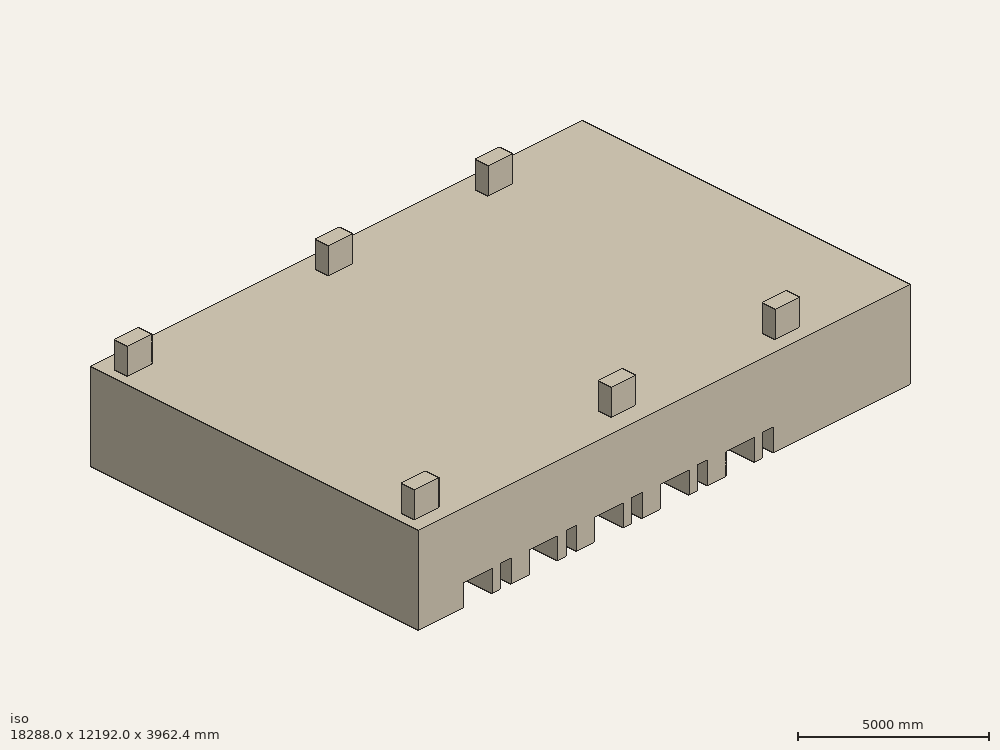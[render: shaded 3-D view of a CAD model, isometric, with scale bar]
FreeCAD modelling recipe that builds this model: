
FCSTD DOCUMENT  (FreeCAD 0.18R14555 (Git shallow))
Label: flow_domain
License: All rights reserved
LicenseURL: http://en.wikipedia.org/wiki/All_rights_reserved
objects: Part::Box×18, Part::MultiFuse×10, Part::Mirroring×1, Part::Cut×1
note: 30 computed .brp shape members not serialized (recipe doc carries the construction recipe); baked Part::Feature solids carry a one-line shape summary decoded from their .brp

FEATURE [Part::Box] Box  label="Room"
  AttacherType = Attacher::AttachEngine3D
  Height = 3048
  Length = 18288
  Width = 12192
FEATURE [Part::Box] Box001  label="Bed 1"
  AttacherType = Attacher::AttachEngine3D
  Height = 762
  Length = 1066.8
  Width = 1981.2
FEATURE [Part::Box] Box002  label="Table 1"
  AttacherType = Attacher::AttachEngine3D
  Height = 798.576
  Length = 396.24
  Placement = pos=(1371.6,0,0) rot=(0,0,1;0rad)
  Width = 396.24
FEATURE [Part::MultiFuse] Fusion  label="Set 1"
  Shapes = -> [Box002,Box001]
FEATURE [Part::Box] Box003  label="Bed 002"
  AttacherType = Attacher::AttachEngine3D
  Height = 762
  Length = 1066.8
  Width = 1981.2
FEATURE [Part::Box] Box004  label="Table 002"
  AttacherType = Attacher::AttachEngine3D
  Height = 798.576
  Length = 396.24
  Placement = pos=(1371.6,0,0) rot=(0,0,1;0rad)
  Width = 396.24
FEATURE [Part::MultiFuse] Fusion001  label="Set 2"
  Placement = pos=(2438.4,0,0) rot=(0,0,1;0rad)
  Shapes = -> [Box004,Box003]
FEATURE [Part::Box] Box005  label="Table 003"
  AttacherType = Attacher::AttachEngine3D
  Height = 798.576
  Length = 396.24
  Placement = pos=(1371.6,0,0) rot=(0,0,1;0rad)
  Width = 396.24
FEATURE [Part::Box] Box006  label="Bed 003"
  AttacherType = Attacher::AttachEngine3D
  Height = 762
  Length = 1066.8
  Width = 1981.2
FEATURE [Part::MultiFuse] Fusion002  label="Set 3"
  Placement = pos=(4876.8,0,0) rot=(0,0,1;0rad)
  Shapes = -> [Box005,Box006]
FEATURE [Part::Box] Box007  label="Bed 004"
  AttacherType = Attacher::AttachEngine3D
  Height = 762
  Length = 1066.8
  Width = 1981.2
FEATURE [Part::Box] Box008  label="Table 004"
  AttacherType = Attacher::AttachEngine3D
  Height = 798.576
  Length = 396.24
  Placement = pos=(1371.6,0,0) rot=(0,0,1;0rad)
  Width = 396.24
FEATURE [Part::MultiFuse] Fusion003  label="Set 4"
  Placement = pos=(7315.2,0,0) rot=(0,0,1;0rad)
  Shapes = -> [Box008,Box007]
FEATURE [Part::Box] Box009  label="Table 005"
  AttacherType = Attacher::AttachEngine3D
  Height = 798.576
  Length = 396.24
  Placement = pos=(1371.6,0,0) rot=(0,0,1;0rad)
  Width = 396.24
FEATURE [Part::Box] Box010  label="Bed 005"
  AttacherType = Attacher::AttachEngine3D
  Height = 762
  Length = 1066.8
  Width = 1981.2
FEATURE [Part::MultiFuse] Fusion004  label="Set 5"
  Placement = pos=(9753.6,0,0) rot=(0,0,1;0rad)
  Shapes = -> [Box009,Box010]
FEATURE [Part::MultiFuse] Fusion005  label="right beds"
  Shapes = -> [Fusion001,Fusion002,Fusion003,Fusion004,Fusion]
FEATURE [Part::Mirroring] Part__Mirroring  label="left beds"
  Base = (0,6096,0)
  Normal = (0,1,0)
  Source = -> Fusion005
FEATURE [Part::Box] Box011  label="Nurse Station"
  AttacherType = Attacher::AttachEngine3D
  Height = 1219.2
  Length = 3048
  Placement = pos=(15240,7620,0) rot=(0,0,1;0rad)
  Width = 4572
FEATURE [Part::Box] Box014  label="Inlet 1"
  AttacherType = Attacher::AttachEngine3D
  Height = 1219.2
  Length = 914.4
  Placement = pos=(13716,11125.2,2743.2) rot=(0,0,1;0rad)
  Width = 487.68
FEATURE [Part::Box] Box015  label="Inlet 2"
  AttacherType = Attacher::AttachEngine3D
  Height = 1219.2
  Length = 914.4
  Placement = pos=(13716,457.2,2743.2) rot=(0,0,1;0rad)
  Width = 487.68
FEATURE [Part::Box] Box018  label="Outlet 2"
  AttacherType = Attacher::AttachEngine3D
  Height = 1219.2
  Length = 914.4
  Placement = pos=(304.8,457.2,2743.2) rot=(0,0,1;0rad)
  Width = 487.68
FEATURE [Part::Box] Box019  label="Outlet 1"
  AttacherType = Attacher::AttachEngine3D
  Height = 1219.2
  Length = 914.4
  Placement = pos=(304.8,11125.2,2743.2) rot=(0,0,1;0rad)
  Width = 487.68
FEATURE [Part::MultiFuse] Fusion006  label="all beds"
  Placement = pos=(1676.4,0,0) rot=(0,0,1;0rad)
  Shapes = -> [Part__Mirroring,Fusion005]
FEATURE [Part::MultiFuse] Fusion008  label="surfaces"
  Shapes = -> [Box011,Fusion006]
FEATURE [Part::Box] Box020  label="Outlet 003"
  AttacherType = Attacher::AttachEngine3D
  Height = 1219.2
  Length = 914.4
  Placement = pos=(7772.4,11125.2,2743.2) rot=(0,0,1;0rad)
  Width = 487.68
FEATURE [Part::Box] Box021  label="Outlet 004"
  AttacherType = Attacher::AttachEngine3D
  Height = 1219.2
  Length = 914.4
  Placement = pos=(7772.4,609.6,2743.2) rot=(0,0,1;0rad)
  Width = 487.68
FEATURE [Part::MultiFuse] Fusion009
  Shapes = -> [Box021,Box014,Box015,Box018,Box019,Box020]
FEATURE [Part::MultiFuse] Fusion010
  Shapes = -> [Box,Fusion009]
FEATURE [Part::Cut] Cut
  Base = -> Fusion010
  Tool = -> Fusion008
